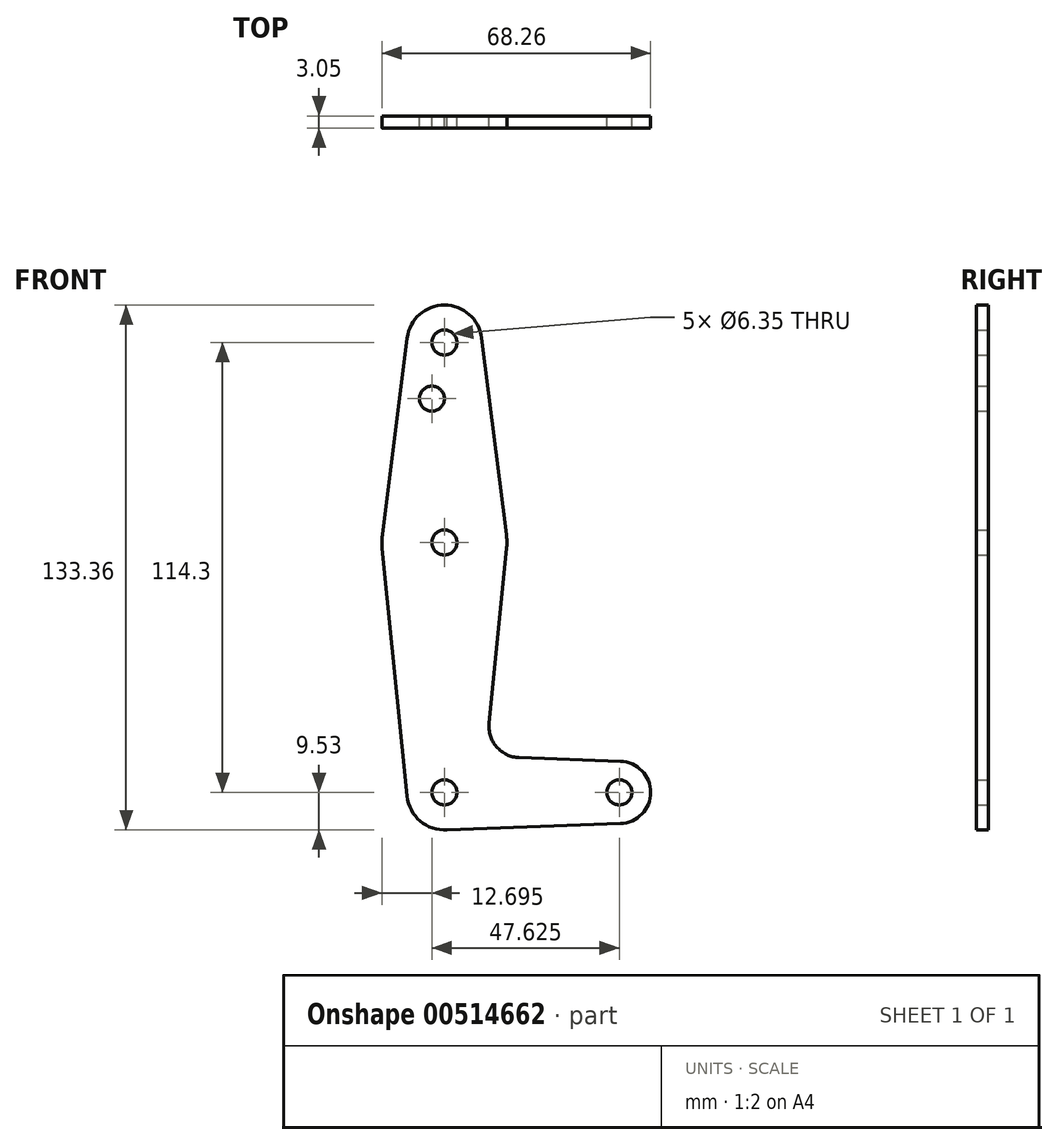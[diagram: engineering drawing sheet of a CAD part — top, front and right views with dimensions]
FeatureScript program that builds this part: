
annotation { "Feature Type Name" : "Feature", "Feature Type Description" : "" }
export const myFeature = defineFeature(function(context is Context, id is Id, definition is map)
    precondition{}
    {
        {
            var Q0;
            Q0=qCreatedBy(makeId("Front.planeOp"),FACE);
            var sketch = newSketch(context, id + "F0", { "sketchPlane" : qUnion([Q0])});
            skCircle(sketch, "E0", {"center": v(0, 0) * mm, "radius": 9.53 * mm});
            skCircle(sketch, "E1", {"center": v(44.45, 0) * mm, "radius": 7.94 * mm});
            skCircle(sketch, "E2", {"center": v(0, 114.3) * mm, "radius": 9.53 * mm});
            skCircle(sketch, "E3", {"center": v(0, 63.5) * mm, "radius": 15.88 * mm});
            skLineSegment(sketch, "E4", {"start": v(0, 114.3) * mm, "end": v(0, 0) * mm, "construction": true});
            skLineSegment(sketch, "E5", {"start": v(44.45, 0) * mm, "end": v(0, 0) * mm, "construction": true});
            skCircle(sketch, "E6", {"center": v(0, 114.3) * mm, "radius": 3.18 * mm});
            skCircle(sketch, "E7", {"center": v(0, 63.5) * mm, "radius": 3.18 * mm});
            skCircle(sketch, "E8", {"center": v(0, 0) * mm, "radius": 3.18 * mm});
            skCircle(sketch, "E9", {"center": v(44.45, 0) * mm, "radius": 3.18 * mm});
            skCircle(sketch, "E10", {"center": v(-3.17, 100.03) * mm, "radius": 3.18 * mm});
            skLineSegment(sketch, "E11", {"start": v(-9.45, 115.5) * mm, "end": v(-15.75, 65.48) * mm});
            skLineSegment(sketch, "E12", {"start": v(9.45, 115.5) * mm, "end": v(15.75, 65.48) * mm});
            skPoint(sketch, "E13.startSnap0", {"position": v(22.23, 0) * mm});
            skLineSegment(sketch, "E14", {"start": v(0, -9.53) * mm, "end": v(44.73, -7.93) * mm});
            skLineSegment(sketch, "E15", {"start": v(18.97, 8.85) * mm, "end": v(44.73, 7.93) * mm});
            skLineSegment(sketch, "E16", {"start": v(-15.8, 61.91) * mm, "end": v(-9.48, -0.95) * mm});
            skLineSegment(sketch, "E17", {"start": v(15.8, 61.91) * mm, "end": v(11.34, 17.59) * mm});
            skPoint(sketch, "E18.newPointA", {"position": v(0, 9.53) * mm});
            skArc(sketch, "E18.filletArc", {"start": v(11.34, 17.59) * mm, "mid": v(13.26, 11.57) * mm, "end": v(18.97, 8.85) * mm});
            skSolve(sketch);
        }
        {
            var Q0;
            Q0 = qSketchRegion(id + "F0", true);
            extrude(context, id + "F1", {"entities" : qUnion([Q0]), "depth" : 3.05 * mm, "offsetDistance" : 25.4 * mm});
        }
    });
